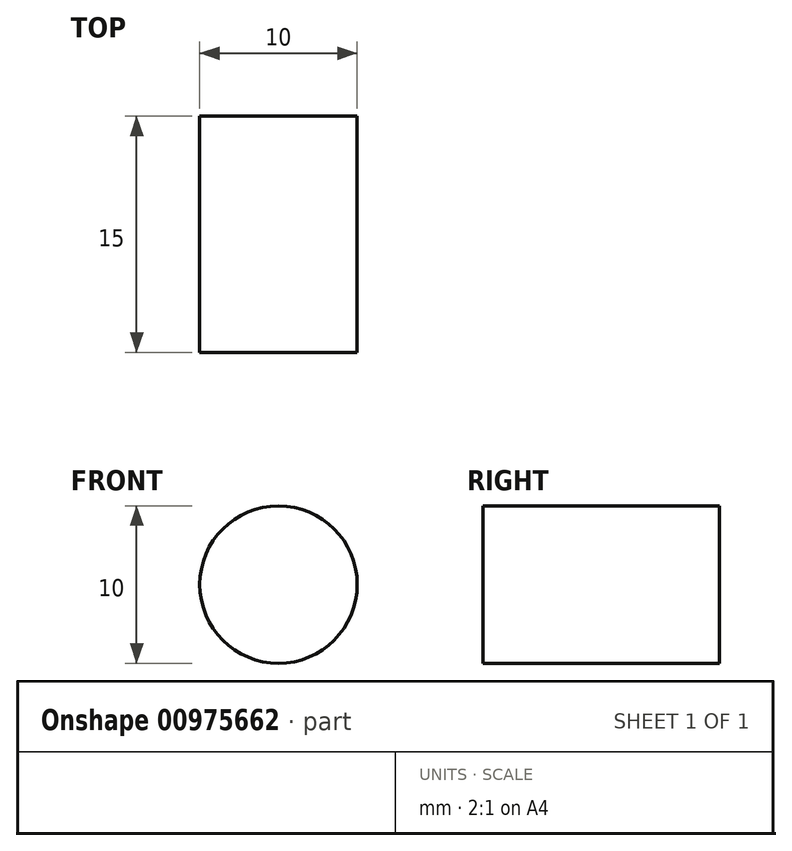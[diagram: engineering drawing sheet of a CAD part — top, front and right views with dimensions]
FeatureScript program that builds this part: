
annotation { "Feature Type Name" : "Feature", "Feature Type Description" : "" }
export const myFeature = defineFeature(function(context is Context, id is Id, definition is map)
    precondition{}
    {
        {
            var Q0;
            Q0=qCreatedBy(makeId("Front.planeOp"),FACE);
            var sketch = newSketch(context, id + "F0", { "sketchPlane" : qUnion([Q0])});
            skCircle(sketch, "E0", {"center": v(0, 0) * mm, "radius": 5 * mm});
            skSolve(sketch);
        }
        {
            var Q0;
            Q0=makeQuery(id+"F0.imprint","IMPRINT",FACE,{"disambiguationData":[TD([[makeQuery(id+"F0.imprint","IMPRINT",EDGE,{"derivedFrom":sQuery(id+"F0.wireOp",EDGE,"E0")}),1.0]])]});
            extrude(context, id + "F1", {"entities" : qUnion([Q0]), "depth" : 15 * mm, "offsetDistance" : 25 * mm});
        }
    });
